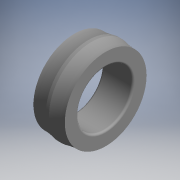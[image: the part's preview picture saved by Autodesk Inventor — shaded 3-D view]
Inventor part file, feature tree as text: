
AUTODESK INVENTOR PART (.ipt)
format: ipt  version: 2017.3 (Build 213256000, 256)  size: 154,112 bytes
history: native  units: mm (DEFAULTED — no unit token found)
features: other x14, revolve x1, sketch x1
ambient origin geometry x8: Origin, YZ Plane, XZ Plane, XY Plane, X Axis, Y Axis, Z Axis, Center Point
bodies: Solid1 (feature_tree)
feature tree (16):
  revolve  "Revolution1"  [1 undecoded]
  other  "NO_GEO_XY"
  other  "NO_GEO_YZ"
  other  "NO_GEO_ZX"
  other  "NO_GEO_X"
  other  "NO_GEO_Y"
  other  "NO_GEO_Z"
  other  "NO_GEO_Center"
  other  "ir_XY"
  other  "ir_YZ"
  other  "ir_ZX"
  other  "ir_X"
  other  "ir_Y"
  other  "ir_Z"
  other  "ir_Center"
  sketch  "Sketch_1"  dims[d0=360.0deg d1=0.0mm]
note: 1 required parameter value undecoded (feature->parameter linkage not recoverable at this tier; creation-order binding heuristic only, values carry confidence <= 0.55)
